# Revit family: VRSE9-24
name_source: partatom
category: Lighting Fixtures
units: mm (PartAtom-declared; Revit-internal decimal feet)

## family parameters
Always vertical = Yes
Cut with Voids When Loaded = No
Host = Floor
Light Source = Yes
Maintain Annotation Orientation = No
OmniClass Number = 23.80.70.11.14.17
OmniClass Title = Direct/Indirect
Part Type = Normal
Room Calculation Point = No
Round Connector Dimension = Use Diameter
Shared = No

## types (3) — shared parameters
Assembly Code = D5020200
Color Filter = 16777215
Default Elevation = 0' - 0"
Description = LED Vandal Resistant Surface
Dimming Lamp Color Temperature Shift = <None>
Emit Shape Visible in Rendering = No
Emit from Rectangle Length = 2' - 1 1/8"
Emit from Rectangle Width = 0' - 9 1/4"
Housing Finish = Extruded Aluminum - Viscor - White
LED Tray Finish = Metal - Viscor - White
Lamp = LED
Length = 2' - 1 1/8"
Lens Finish = Polycarbonate - Viscor - Frosted
Manufacturer = CERTOLUX by VISCOR
Model = VRSE9-24
Tilt Angle = -90.00°
URL = https://viscor.com
Voltage = 120 V
Width = 0' - 9 1/4"

## per-type parameters (varying)
| type | Apparent Load | Lamp Wattage | Photometric Web File |
| VRSE9-48-LED840K035LUNV-DPP | 26 VA | 26 VA | VRSE9-24-LED840K035LUNV-DPP.ies |
| VRSE9-24-LED840K025LUNV-DPP | 18 VA | 18 VA | VRSE9-24-LED840K025LUNV-DPP.ies |
| VRSE9-24-LED840K055LUNV-DPP | 42 VA | 42 VA | VRSE9-24-LED840K055LUNV-DPP.ies |

## geometry (parser evidence)
native form markers: Sweep x2
no freeform markers — native parametric forms only
